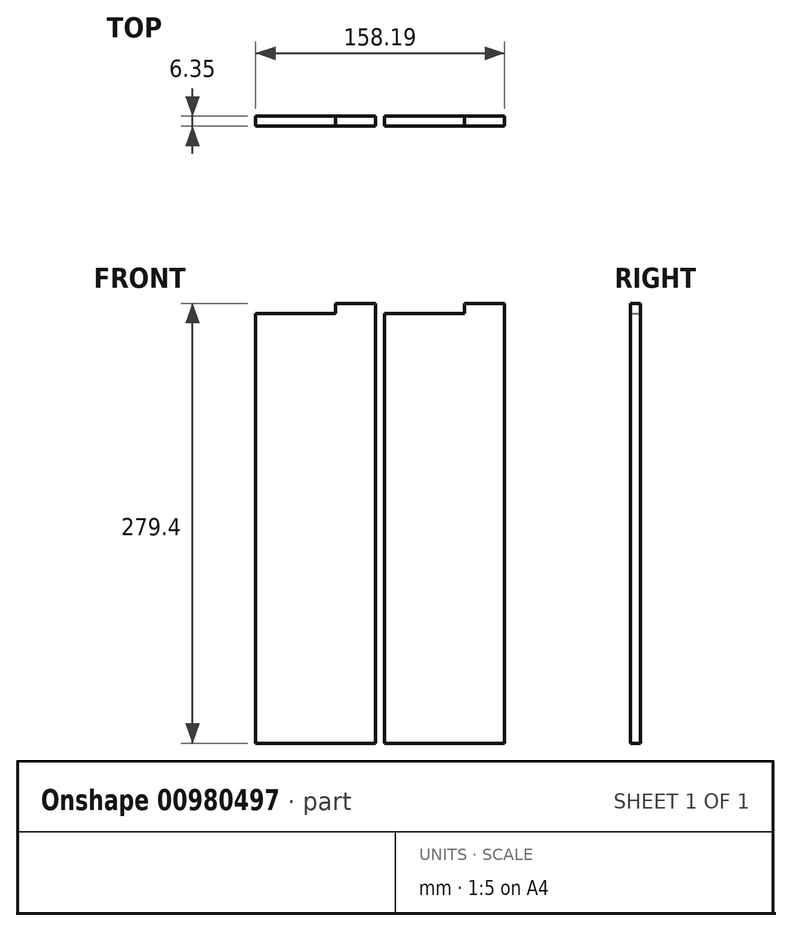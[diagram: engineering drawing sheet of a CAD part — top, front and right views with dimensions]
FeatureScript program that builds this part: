
annotation { "Feature Type Name" : "Feature", "Feature Type Description" : "" }
export const myFeature = defineFeature(function(context is Context, id is Id, definition is map)
    precondition{}
    {
        {
            var Q0;
            Q0=qCreatedBy(makeId("Front.planeOp"),FACE);
            var sketch = newSketch(context, id + "F0", { "sketchPlane" : qUnion([Q0])});
            skLineSegment(sketch, "E0", {"start": v(99.37, 198.7) * mm, "end": v(99.37, 198.7) * mm});
            skLineSegment(sketch, "E1", {"start": v(99.37, 198.7) * mm, "end": v(99.37, 122.5) * mm});
            skLineSegment(sketch, "E2", {"start": v(99.37, 122.5) * mm, "end": v(-345.13, 122.5) * mm});
            skLineSegment(sketch, "E3", {"start": v(-345.13, 122.5) * mm, "end": v(-345.13, 198.7) * mm});
            skLineSegment(sketch, "E4", {"start": v(-345.13, 198.7) * mm, "end": v(99.37, 198.7) * mm});
            skLineSegment(sketch, "E5", {"start": v(-345.13, 198.7) * mm, "end": v(-345.13, 122.5) * mm});
            skLineSegment(sketch, "E6", {"start": v(-344.55, 39.42) * mm, "end": v(-344.55, 115.62) * mm});
            skLineSegment(sketch, "E7", {"start": v(-344.55, 115.62) * mm, "end": v(182.5, 115.62) * mm});
            skLineSegment(sketch, "E8", {"start": v(182.5, 115.62) * mm, "end": v(182.5, 39.42) * mm});
            skLineSegment(sketch, "E9", {"start": v(182.5, 39.42) * mm, "end": v(182.5, 39.42) * mm});
            skLineSegment(sketch, "E10", {"start": v(182.5, 39.42) * mm, "end": v(-344.55, 39.42) * mm});
            skLineSegment(sketch, "E11", {"start": v(-27.75, 39.42) * mm, "end": v(-27.75, 77.52) * mm});
            skLineSegment(sketch, "E12", {"start": v(-27.46, 77.52) * mm, "end": v(-21.11, 77.52) * mm});
            skLineSegment(sketch, "E13", {"start": v(-21.11, 77.52) * mm, "end": v(-21.11, 39.42) * mm});
            skLineSegment(sketch, "E14", {"start": v(-21.11, 39.42) * mm, "end": v(-21.11, 39.42) * mm});
            skLineSegment(sketch, "E15", {"start": v(-21.11, 39.42) * mm, "end": v(-27.46, 39.42) * mm});
            skLineSegment(sketch, "E16", {"start": v(-97.25, 39.42) * mm, "end": v(-97.25, 77.52) * mm});
            skLineSegment(sketch, "E17", {"start": v(-97.6, 77.52) * mm, "end": v(-91.25, 77.52) * mm});
            skLineSegment(sketch, "E18", {"start": v(-91.25, 77.52) * mm, "end": v(-91.25, 39.42) * mm});
            skLineSegment(sketch, "E19", {"start": v(-91.25, 39.42) * mm, "end": v(-91.25, 39.42) * mm});
            skLineSegment(sketch, "E20", {"start": v(-91.25, 39.42) * mm, "end": v(-97.6, 39.42) * mm});
            skLineSegment(sketch, "E21", {"start": v(-224.25, 39.42) * mm, "end": v(-224.25, 77.52) * mm});
            skLineSegment(sketch, "E22", {"start": v(-224.25, 77.52) * mm, "end": v(-217.9, 77.52) * mm});
            skLineSegment(sketch, "E23", {"start": v(-217.9, 77.52) * mm, "end": v(-217.9, 39.42) * mm});
            skLineSegment(sketch, "E24", {"start": v(-217.9, 39.42) * mm, "end": v(-217.9, 39.42) * mm});
            skLineSegment(sketch, "E25", {"start": v(-217.9, 39.42) * mm, "end": v(-224.25, 39.42) * mm});
            skLineSegment(sketch, "E26", {"start": v(-344.55, -39.95) * mm, "end": v(-344.55, 36.25) * mm});
            skLineSegment(sketch, "E27", {"start": v(-344.55, 36.25) * mm, "end": v(182.5, 36.25) * mm});
            skLineSegment(sketch, "E28", {"start": v(182.5, 36.25) * mm, "end": v(182.5, -39.95) * mm});
            skLineSegment(sketch, "E29", {"start": v(182.5, -39.95) * mm, "end": v(182.5, -39.95) * mm});
            skLineSegment(sketch, "E30", {"start": v(182.5, -39.96) * mm, "end": v(-344.55, -39.96) * mm});
            skLineSegment(sketch, "E31", {"start": v(-224.25, -39.95) * mm, "end": v(-224.25, -1.85) * mm});
            skLineSegment(sketch, "E32", {"start": v(-224.25, -1.85) * mm, "end": v(-217.9, -1.85) * mm});
            skLineSegment(sketch, "E33", {"start": v(-217.9, -1.85) * mm, "end": v(-217.9, -39.95) * mm});
            skLineSegment(sketch, "E34", {"start": v(-217.9, -39.95) * mm, "end": v(-217.9, -39.95) * mm});
            skLineSegment(sketch, "E35", {"start": v(-217.9, -39.95) * mm, "end": v(-224.25, -39.95) * mm});
            skLineSegment(sketch, "E36", {"start": v(-97.25, -39.95) * mm, "end": v(-97.25, -1.85) * mm});
            skLineSegment(sketch, "E37", {"start": v(-97.25, -1.85) * mm, "end": v(-90.9, -1.85) * mm});
            skLineSegment(sketch, "E38", {"start": v(-90.9, -1.85) * mm, "end": v(-90.9, -39.95) * mm});
            skLineSegment(sketch, "E39", {"start": v(-90.9, -39.95) * mm, "end": v(-90.9, -39.95) * mm});
            skLineSegment(sketch, "E40", {"start": v(-90.9, -39.95) * mm, "end": v(-97.19, -39.95) * mm});
            skLineSegment(sketch, "E41", {"start": v(-262.7, -119.33) * mm, "end": v(-262.7, -81.23) * mm});
            skLineSegment(sketch, "E42", {"start": v(-262.7, -81.23) * mm, "end": v(-256.35, -81.23) * mm});
            skLineSegment(sketch, "E43", {"start": v(-256.35, -81.23) * mm, "end": v(-256.35, -119.33) * mm});
            skLineSegment(sketch, "E44", {"start": v(-256.35, -119.33) * mm, "end": v(-256.35, -119.33) * mm});
            skLineSegment(sketch, "E45", {"start": v(-256.35, -119.33) * mm, "end": v(-262.7, -119.33) * mm});
            skLineSegment(sketch, "E46", {"start": v(-192.85, -119.33) * mm, "end": v(-192.85, -81.23) * mm});
            skLineSegment(sketch, "E47", {"start": v(-192.85, -81.23) * mm, "end": v(-186.5, -81.23) * mm});
            skLineSegment(sketch, "E48", {"start": v(-186.5, -81.23) * mm, "end": v(-186.5, -119.33) * mm});
            skLineSegment(sketch, "E49", {"start": v(-186.5, -119.33) * mm, "end": v(-186.5, -119.33) * mm});
            skLineSegment(sketch, "E50", {"start": v(-186.5, -119.33) * mm, "end": v(-192.85, -119.33) * mm});
            skLineSegment(sketch, "E51", {"start": v(10.14, -119.33) * mm, "end": v(10.14, -81.23) * mm});
            skLineSegment(sketch, "E52", {"start": v(10.14, -81.23) * mm, "end": v(16.49, -81.23) * mm});
            skLineSegment(sketch, "E53", {"start": v(16.49, -81.23) * mm, "end": v(16.49, -119.33) * mm});
            skLineSegment(sketch, "E54", {"start": v(16.49, -119.33) * mm, "end": v(16.49, -119.33) * mm});
            skLineSegment(sketch, "E55", {"start": v(16.49, -119.33) * mm, "end": v(10.14, -119.33) * mm});
            skLineSegment(sketch, "E56", {"start": v(-141.7, -198.35) * mm, "end": v(-141.7, -160.25) * mm});
            skLineSegment(sketch, "E57", {"start": v(-141.7, -160.25) * mm, "end": v(-135.35, -160.25) * mm});
            skLineSegment(sketch, "E58", {"start": v(-135.35, -160.25) * mm, "end": v(-135.35, -198.35) * mm});
            skLineSegment(sketch, "E59", {"start": v(-135.35, -198.35) * mm, "end": v(-135.35, -198.35) * mm});
            skLineSegment(sketch, "E60", {"start": v(-135.35, -198.35) * mm, "end": v(-141.7, -198.35) * mm});
            skLineSegment(sketch, "E61", {"start": v(-325.85, -93.9) * mm, "end": v(-325.85, -43.13) * mm});
            skLineSegment(sketch, "E62", {"start": v(-325.85, -43.13) * mm, "end": v(-122.65, -43.13) * mm});
            skLineSegment(sketch, "E63", {"start": v(-122.65, -43.13) * mm, "end": v(-122.65, -93.9) * mm});
            skLineSegment(sketch, "E64", {"start": v(-122.65, -119.3) * mm, "end": v(-325.85, -119.3) * mm});
            skLineSegment(sketch, "E65", {"start": v(345.13, 106.1) * mm, "end": v(345.13, -166.95) * mm});
            skLineSegment(sketch, "E66", {"start": v(345.13, -166.95) * mm, "end": v(268.93, -166.95) * mm});
            skLineSegment(sketch, "E67", {"start": v(268.93, -166.95) * mm, "end": v(268.93, 106.1) * mm});
            skLineSegment(sketch, "E68", {"start": v(268.93, 106.1) * mm, "end": v(319.73, 106.1) * mm});
            skLineSegment(sketch, "E69", {"start": v(263.14, 106.1) * mm, "end": v(263.14, -166.95) * mm});
            skLineSegment(sketch, "E70", {"start": v(263.14, -166.95) * mm, "end": v(186.94, -166.95) * mm});
            skLineSegment(sketch, "E71", {"start": v(186.94, -166.95) * mm, "end": v(186.94, 106.1) * mm});
            skLineSegment(sketch, "E72", {"start": v(186.94, 106.1) * mm, "end": v(237.74, 106.1) * mm});
            skLineSegment(sketch, "E73", {"start": v(80.34, -68.53) * mm, "end": v(80.34, -119.33) * mm});
            skLineSegment(sketch, "E74", {"start": v(80.34, -119.33) * mm, "end": v(-53, -119.33) * mm});
            skLineSegment(sketch, "E75", {"start": v(-53, -119.33) * mm, "end": v(-53, -43.13) * mm});
            skLineSegment(sketch, "E76", {"start": v(-53, -43.13) * mm, "end": v(80.34, -43.13) * mm});
            skLineSegment(sketch, "E77", {"start": v(55.5, -147.9) * mm, "end": v(55.5, -198.7) * mm});
            skLineSegment(sketch, "E78", {"start": v(55.5, -198.7) * mm, "end": v(-344.55, -198.7) * mm});
            skLineSegment(sketch, "E79", {"start": v(-344.55, -198.7) * mm, "end": v(-344.55, -122.5) * mm});
            skLineSegment(sketch, "E80", {"start": v(-344.55, -122.5) * mm, "end": v(55.5, -122.5) * mm});
            skLineSegment(sketch, "E81", {"start": v(237.74, 106.1) * mm, "end": v(237.74, 112.45) * mm});
            skLineSegment(sketch, "E82", {"start": v(237.74, 112.45) * mm, "end": v(263.14, 112.45) * mm});
            skLineSegment(sketch, "E83", {"start": v(263.14, 112.45) * mm, "end": v(263.14, 106.1) * mm});
            skLineSegment(sketch, "E84", {"start": v(319.73, 106.1) * mm, "end": v(319.73, 112.45) * mm});
            skLineSegment(sketch, "E85", {"start": v(319.73, 112.45) * mm, "end": v(345.13, 112.45) * mm});
            skLineSegment(sketch, "E86", {"start": v(345.13, 112.45) * mm, "end": v(345.13, 106.1) * mm});
            skLineSegment(sketch, "E87", {"start": v(80.34, -43.13) * mm, "end": v(86.7, -43.13) * mm});
            skLineSegment(sketch, "E88", {"start": v(86.7, -43.13) * mm, "end": v(86.7, -68.53) * mm});
            skLineSegment(sketch, "E89", {"start": v(86.7, -68.53) * mm, "end": v(80.34, -68.53) * mm});
            skLineSegment(sketch, "E90", {"start": v(-122.65, -93.9) * mm, "end": v(-116.3, -93.9) * mm});
            skLineSegment(sketch, "E91", {"start": v(-116.3, -93.9) * mm, "end": v(-116.3, -119.3) * mm});
            skLineSegment(sketch, "E92", {"start": v(-116.3, -119.3) * mm, "end": v(-122.65, -119.3) * mm});
            skLineSegment(sketch, "E93", {"start": v(-325.85, -119.3) * mm, "end": v(-332.2, -119.3) * mm});
            skLineSegment(sketch, "E94", {"start": v(-332.2, -119.3) * mm, "end": v(-332.2, -93.9) * mm});
            skLineSegment(sketch, "E95", {"start": v(-332.2, -93.9) * mm, "end": v(-325.85, -93.9) * mm});
            skLineSegment(sketch, "E96", {"start": v(55.5, -122.5) * mm, "end": v(61.85, -122.5) * mm});
            skLineSegment(sketch, "E97", {"start": v(61.85, -122.5) * mm, "end": v(61.85, -147.9) * mm});
            skLineSegment(sketch, "E98", {"start": v(61.85, -147.9) * mm, "end": v(55.5, -147.9) * mm});
            skLineSegment(sketch, "E99", {"start": v(-281.87, 122.62) * mm, "end": v(-281.87, 160.72) * mm});
            skLineSegment(sketch, "E100", {"start": v(-281.87, 160.72) * mm, "end": v(-275.52, 160.72) * mm});
            skLineSegment(sketch, "E101", {"start": v(-275.52, 160.72) * mm, "end": v(-275.52, 122.62) * mm});
            skLineSegment(sketch, "E102", {"start": v(-275.52, 122.62) * mm, "end": v(-275.52, 122.62) * mm});
            skLineSegment(sketch, "E103", {"start": v(-275.52, 122.62) * mm, "end": v(-281.87, 122.62) * mm});
            skLineSegment(sketch, "E104", {"start": v(-97.19, -39.95) * mm, "end": v(-97.25, -39.95) * mm});
            skLineSegment(sketch, "E105.bottom", {"start": v(-2.59, 160.6) * mm, "end": v(3.76, 160.6) * mm});
            skLineSegment(sketch, "E105.top", {"start": v(-2.59, 122.5) * mm, "end": v(3.76, 122.5) * mm});
            skLineSegment(sketch, "E105.left", {"start": v(-2.59, 160.6) * mm, "end": v(-2.59, 122.5) * mm});
            skLineSegment(sketch, "E105.right", {"start": v(3.76, 160.6) * mm, "end": v(3.76, 122.5) * mm});
            skLineSegment(sketch, "E106.bottom", {"start": v(-212.14, 160.55) * mm, "end": v(-205.79, 160.55) * mm});
            skLineSegment(sketch, "E106.top", {"start": v(-212.14, 122.45) * mm, "end": v(-205.79, 122.45) * mm});
            skLineSegment(sketch, "E106.left", {"start": v(-212.14, 160.55) * mm, "end": v(-212.14, 122.45) * mm});
            skLineSegment(sketch, "E106.right", {"start": v(-205.79, 160.55) * mm, "end": v(-205.79, 122.45) * mm});
            skSolve(sketch);
        }
        {
            var Q0;
            Q0=makeQuery(id+"F0.imprint","IMPRINT",FACE,{"disambiguationData":[TD([[makeQuery(id+"F0.imprint","IMPRINT",EDGE,{"derivedFrom":sQuery(id+"F0.wireOp",EDGE,"ba393244-6abe-4dcc-b71a-991447f8cf6d")}),1.0]])]});
            var Q1;
            {var subQ2=sQuery(id+"F0.wireOp",EDGE,"E6");Q1=makeQuery(id+"F0.imprint","IMPRINT",FACE,{"disambiguationData":[TD([[makeQuery(id+"F0.imprint","IMPRINT",EDGE,{"derivedFrom":subQ2}),-1.0]])]});}
            var Q2;
            {var subQ2=sQuery(id+"F0.wireOp",EDGE,"E26");Q2=makeQuery(id+"F0.imprint","IMPRINT",FACE,{"disambiguationData":[TD([[makeQuery(id+"F0.imprint","IMPRINT",EDGE,{"derivedFrom":subQ2}),-1.0]])]});}
            var Q3;
            {var subQ5=sQuery(id+"F0.wireOp",EDGE,"E42");Q3=makeQuery(id+"F0.imprint","IMPRINT",FACE,{"disambiguationData":[TD([[makeQuery(id+"F0.imprint","IMPRINT",EDGE,{"derivedFrom":subQ5}),1.0]])]});}
            var Q4;
            Q4=makeQuery(id+"F0.imprint","IMPRINT",FACE,{"disambiguationData":[TD([[makeQuery(id+"F0.imprint","IMPRINT",EDGE,{"derivedFrom":sQuery(id+"F0.wireOp",EDGE,"E51")}),1.0]])]});
            var Q5;
            Q5=makeQuery(id+"F0.imprint","IMPRINT",FACE,{"disambiguationData":[TD([[makeQuery(id+"F0.imprint","IMPRINT",EDGE,{"derivedFrom":sQuery(id+"F0.wireOp",EDGE,"E56")}),1.0]])]});
            var Q6;
            Q6=makeQuery(id+"F0.imprint","IMPRINT",FACE,{"disambiguationData":[TD([[makeQuery(id+"F0.imprint","IMPRINT",EDGE,{"derivedFrom":sQuery(id+"F0.wireOp",EDGE,"E69")}),-1.0]])]});
            var Q7;
            Q7=makeQuery(id+"F0.imprint","IMPRINT",FACE,{"disambiguationData":[TD([[makeQuery(id+"F0.imprint","IMPRINT",EDGE,{"derivedFrom":sQuery(id+"F0.wireOp",EDGE,"E65")}),-1.0]])]});
            extrude(context, id + "F1", {"entities" : qUnion([Q0, Q1, Q2, Q3, Q4, Q5, Q6, Q7]), "depth" : 6.35 * mm, "offsetDistance" : 25.4 * mm});
        }
    });
